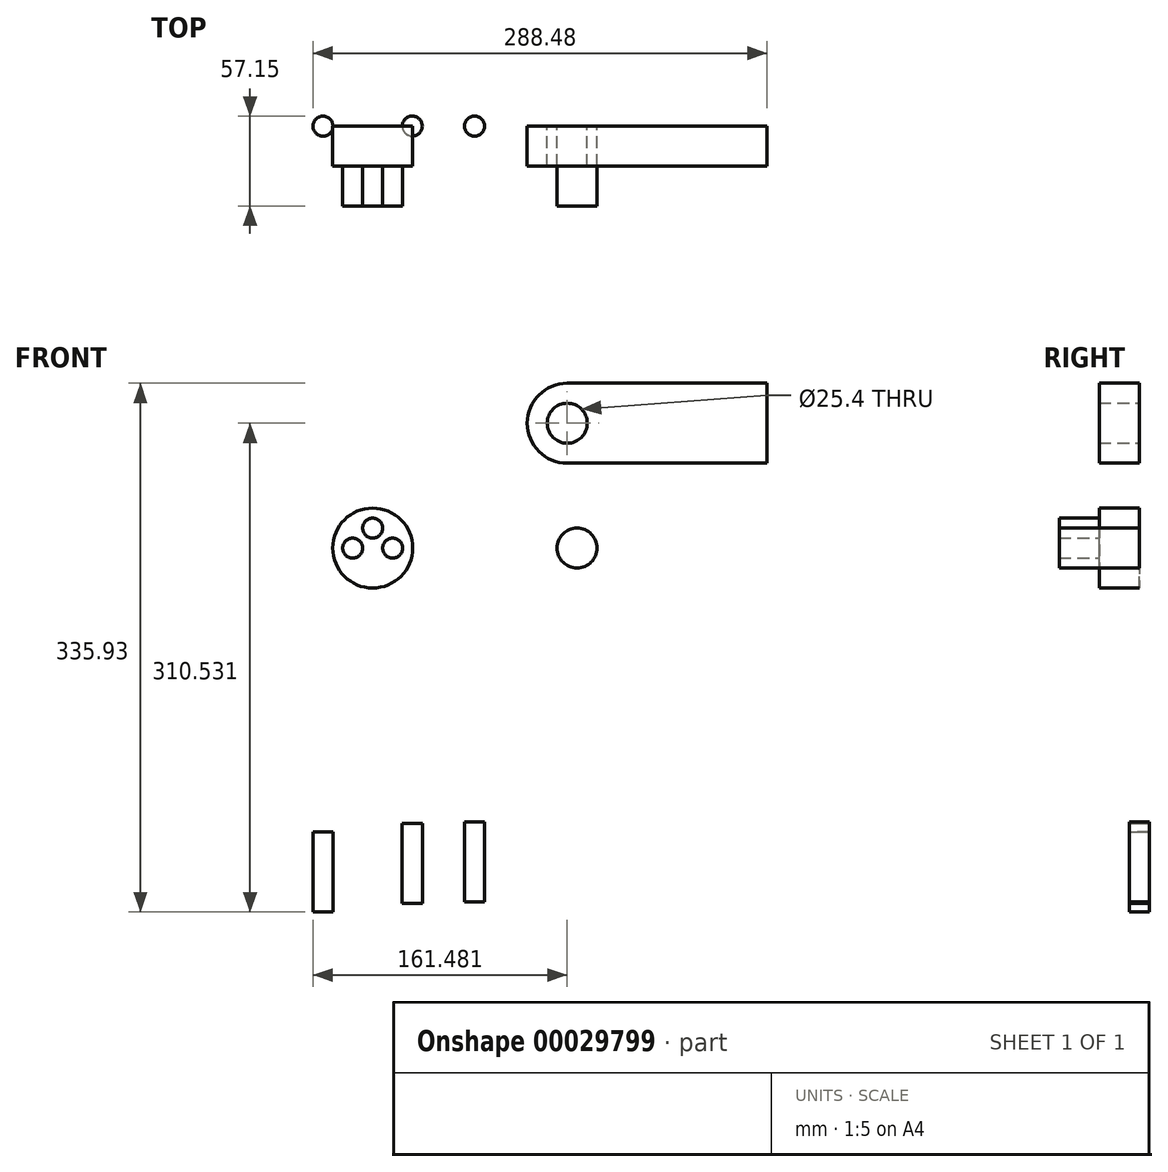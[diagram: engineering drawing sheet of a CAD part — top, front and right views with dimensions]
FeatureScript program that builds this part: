
annotation { "Feature Type Name" : "Feature", "Feature Type Description" : "" }
export const myFeature = defineFeature(function(context is Context, id is Id, definition is map)
    precondition{}
    {
        {
            var Q0;
            Q0=qCreatedBy(makeId("Front.planeOp"),FACE);
            var sketch = newSketch(context, id + "F0", { "sketchPlane" : qUnion([Q0])});
            skCircle(sketch, "E0", {"center": v(0, 0) * mm, "radius": 12.7 * mm});
            skLineSegment(sketch, "E1", {"start": v(0, 0) * mm, "end": v(0, 12.7) * mm});
            skLineSegment(sketch, "E2.bottom", {"start": v(-6.25, 104.71) * mm, "end": v(120.75, 104.71) * mm});
            skLineSegment(sketch, "E2.top", {"start": v(-6.25, 53.91) * mm, "end": v(120.75, 53.91) * mm});
            skLineSegment(sketch, "E2.left", {"start": v(-31.65, 79.31) * mm, "end": v(-31.65, 79.31) * mm});
            skLineSegment(sketch, "E2.right", {"start": v(120.75, 104.71) * mm, "end": v(120.75, 53.91) * mm});
            skPoint(sketch, "E3.visualSharp", {"position": v(-31.65, 104.71) * mm});
            skArc(sketch, "E3.filletArc", {"start": v(-6.25, 104.71) * mm, "mid": v(-24.2, 97.27) * mm, "end": v(-31.65, 79.31) * mm});
            skPoint(sketch, "E4.visualSharp", {"position": v(-31.65, 53.91) * mm});
            skArc(sketch, "E4.filletArc", {"start": v(-31.65, 79.31) * mm, "mid": v(-24.2, 61.35) * mm, "end": v(-6.25, 53.91) * mm});
            skCircle(sketch, "E5", {"center": v(-6.25, 79.31) * mm, "radius": 12.7 * mm});
            skLineSegment(sketch, "E6", {"start": v(-6.25, 79.31) * mm, "end": v(0, 90.37) * mm});
            skSolve(sketch);
        }
        {
            var Q0;
            Q0=makeQuery(id+"F0.imprint","IMPRINT",FACE,{"disambiguationData":[TD([[makeQuery(id+"F0.imprint","IMPRINT",EDGE,{"derivedFrom":sQuery(id+"F0.wireOp",EDGE,"E2.bottom")}),-1.0]])]});
            extrude(context, id + "F1", {"entities" : qUnion([Q0]), "depth" : 25.4 * mm});
        }
        {
            var Q0;
            Q0=qCreatedBy(makeId("Front.planeOp"),FACE);
            var sketch = newSketch(context, id + "F2", { "sketchPlane" : qUnion([Q0])});
            skLineSegment(sketch, "E7.bottom", {"start": v(-161.38, -180.42) * mm, "end": v(-155.03, -180.42) * mm});
            skLineSegment(sketch, "E7.top", {"start": v(-161.38, -231.22) * mm, "end": v(-155.03, -231.22) * mm});
            skLineSegment(sketch, "E7.left", {"start": v(-161.38, -180.42) * mm, "end": v(-161.38, -231.22) * mm});
            skLineSegment(sketch, "E7.right", {"start": v(-155.03, -180.42) * mm, "end": v(-155.03, -231.22) * mm});
            skLineSegment(sketch, "E8.bottom", {"start": v(-104.67, -225.58) * mm, "end": v(-98.32, -225.58) * mm});
            skLineSegment(sketch, "E8.top", {"start": v(-104.67, -174.78) * mm, "end": v(-98.32, -174.78) * mm});
            skLineSegment(sketch, "E8.left", {"start": v(-104.67, -225.58) * mm, "end": v(-104.67, -174.78) * mm});
            skLineSegment(sketch, "E8.right", {"start": v(-98.32, -225.58) * mm, "end": v(-98.32, -174.78) * mm});
            skLineSegment(sketch, "E9.bottom", {"start": v(-58.8, -224.74) * mm, "end": v(-65.15, -224.74) * mm});
            skLineSegment(sketch, "E9.top", {"start": v(-58.8, -173.94) * mm, "end": v(-65.15, -173.94) * mm});
            skLineSegment(sketch, "E9.left", {"start": v(-58.8, -224.74) * mm, "end": v(-58.8, -173.94) * mm});
            skLineSegment(sketch, "E9.right", {"start": v(-65.15, -224.74) * mm, "end": v(-65.15, -173.94) * mm});
            skSolve(sketch);
        }
        {
            var Q0;
            Q0=makeQuery(id+"F2.imprint","IMPRINT",FACE,{"disambiguationData":[TD([[makeQuery(id+"F2.imprint","IMPRINT",EDGE,{"derivedFrom":sQuery(id+"F2.wireOp",EDGE,"E7.bottom")}),-1.0]])]});
            var Q1;
            Q1=sQuery(id+"F2.wireOp",EDGE,"E7.left");
            revolve(context, id + "F3", {"entities" : qUnion([Q0]), "axis" : qUnion([Q1]), "revolveType" : RevolveType.FULL});
        }
        {
            var Q0;
            Q0=makeQuery(id+"F2.imprint","IMPRINT",FACE,{"disambiguationData":[TD([[makeQuery(id+"F2.imprint","IMPRINT",EDGE,{"derivedFrom":sQuery(id+"F2.wireOp",EDGE,"E8.bottom")}),1.0]])]});
            var Q1;
            Q1=sQuery(id+"F2.wireOp",EDGE,"E8.left");
            revolve(context, id + "F4", {"entities" : qUnion([Q0]), "axis" : qUnion([Q1]), "revolveType" : RevolveType.FULL});
        }
        {
            var Q0;
            Q0=makeQuery(id+"F2.imprint","IMPRINT",FACE,{"disambiguationData":[TD([[makeQuery(id+"F2.imprint","IMPRINT",EDGE,{"derivedFrom":sQuery(id+"F2.wireOp",EDGE,"E9.bottom")}),-1.0]])]});
            var Q1;
            Q1=sQuery(id+"F2.wireOp",EDGE,"E9.right");
            revolve(context, id + "F5", {"entities" : qUnion([Q0]), "axis" : qUnion([Q1]), "revolveType" : RevolveType.FULL});
        }
        {
            var Q0;
            Q0=makeQuery(id+"F0.imprint","IMPRINT",FACE,{"disambiguationData":[TD([[makeQuery(id+"F0.imprint","IMPRINT",EDGE,{"derivedFrom":sQuery(id+"F0.wireOp",EDGE,"E0")}),1.0]])]});
            extrude(context, id + "F6", {"entities" : qUnion([Q0]), "depth" : 50.8 * mm});
        }
        {
            var Q0;
            Q0=qCreatedBy(makeId("Front.planeOp"),FACE);
            var sketch = newSketch(context, id + "F7", { "sketchPlane" : qUnion([Q0])});
            skCircle(sketch, "E10", {"center": v(-129.83, 0) * mm, "radius": 25.4 * mm});
            skLineSegment(sketch, "E11", {"start": v(-129.83, 0) * mm, "end": v(-129.83, 25.4) * mm});
            skLineSegment(sketch, "E12", {"start": v(-129.83, 0) * mm, "end": v(-104.43, 0) * mm});
            skLineSegment(sketch, "E13", {"start": v(-129.83, 0) * mm, "end": v(-155.23, 0) * mm});
            skLineSegment(sketch, "E14", {"start": v(-129.83, 0) * mm, "end": v(-129.83, -25.4) * mm});
            skCircle(sketch, "E15", {"center": v(-129.83, 12.7) * mm, "radius": 6.35 * mm});
            skCircle(sketch, "E16", {"center": v(-117.13, 0) * mm, "radius": 6.35 * mm});
            skCircle(sketch, "E17", {"center": v(-142.53, 0) * mm, "radius": 6.35 * mm});
            skLineSegment(sketch, "E18", {"start": v(-142.53, 0) * mm, "end": v(-142.53, 6.35) * mm});
            skLineSegment(sketch, "E19", {"start": v(-129.83, 12.7) * mm, "end": v(-123.48, 12.7) * mm});
            skLineSegment(sketch, "E20", {"start": v(-117.13, 0) * mm, "end": v(-117.13, 6.35) * mm});
            skSolve(sketch);
        }
        {
            var Q0;
            {var subQ6=sQuery(id+"F7.wireOp",EDGE,"E11");var subQ10=sQuery(id+"F7.wireOp",EDGE,"E10");var subQ13=makeQuery(id+"F7.imprint","INTERSECT",VERTEX,{"derivedFrom":[subQ10,subQ6]});Q0=makeQuery(id+"F7.imprint","IMPRINT",FACE,{"disambiguationData":[TD([[makeQuery(id+"F7.imprint","IMPRINT",EDGE,{"disambiguationData":[TD([[subQ13,1.0]])],"derivedFrom":subQ10}),1.0]])]});}
            var Q1;
            {var subQ4=sQuery(id+"F7.wireOp",EDGE,"E14");Q1=makeQuery(id+"F7.imprint","IMPRINT",FACE,{"disambiguationData":[TD([[makeQuery(id+"F7.imprint","IMPRINT",EDGE,{"derivedFrom":subQ4}),1.0]])]});}
            var Q2;
            {var subQ4=sQuery(id+"F7.wireOp",EDGE,"E14");Q2=makeQuery(id+"F7.imprint","IMPRINT",FACE,{"disambiguationData":[TD([[makeQuery(id+"F7.imprint","IMPRINT",EDGE,{"derivedFrom":subQ4}),-1.0]])]});}
            var Q3;
            {var subQ6=sQuery(id+"F7.wireOp",EDGE,"E11");var subQ9=sQuery(id+"F7.wireOp",EDGE,"E10");var subQ12=makeQuery(id+"F7.imprint","INTERSECT",VERTEX,{"derivedFrom":[subQ9,subQ6]});Q3=makeQuery(id+"F7.imprint","IMPRINT",FACE,{"disambiguationData":[TD([[makeQuery(id+"F7.imprint","IMPRINT",EDGE,{"disambiguationData":[TD([[subQ12,-1.0]])],"derivedFrom":subQ9}),1.0]])]});}
            extrude(context, id + "F8", {"entities" : qUnion([Q0, Q1, Q2, Q3]), "depth" : 25.4 * mm});
        }
        {
            var Q0;
            {var subQ0=sQuery(id+"F7.wireOp",EDGE,"E20");Q0=makeQuery(id+"F7.imprint","IMPRINT",FACE,{"disambiguationData":[TD([[makeQuery(id+"F7.imprint","IMPRINT",EDGE,{"derivedFrom":subQ0}),-1.0]])]});}
            var Q1;
            {var subQ0=sQuery(id+"F7.wireOp",EDGE,"E20");Q1=makeQuery(id+"F7.imprint","IMPRINT",FACE,{"disambiguationData":[TD([[makeQuery(id+"F7.imprint","IMPRINT",EDGE,{"derivedFrom":subQ0}),1.0]])]});}
            var Q2;
            {var subQ1=sQuery(id+"F7.wireOp",EDGE,"E12");var subQ4=makeQuery(id+"F7.imprint","INTERSECT",VERTEX,{"derivedFrom":[subQ1,sQuery(id+"F7.wireOp",EDGE,"E20")]});Q2=makeQuery(id+"F7.imprint","IMPRINT",FACE,{"disambiguationData":[TD([[makeQuery(id+"F7.imprint","IMPRINT",EDGE,{"disambiguationData":[TD([[subQ4,1.0]])],"derivedFrom":subQ1}),-1.0]])]});}
            var Q3;
            {var subQ0=sQuery(id+"F7.wireOp",EDGE,"E19");Q3=makeQuery(id+"F7.imprint","IMPRINT",FACE,{"disambiguationData":[TD([[makeQuery(id+"F7.imprint","IMPRINT",EDGE,{"derivedFrom":subQ0}),1.0]])]});}
            var Q4;
            {var subQ1=sQuery(id+"F7.wireOp",EDGE,"E11");var subQ4=makeQuery(id+"F7.imprint","INTERSECT",VERTEX,{"derivedFrom":[subQ1,sQuery(id+"F7.wireOp",EDGE,"E19")]});Q4=makeQuery(id+"F7.imprint","IMPRINT",FACE,{"disambiguationData":[TD([[makeQuery(id+"F7.imprint","IMPRINT",EDGE,{"disambiguationData":[TD([[subQ4,1.0]])],"derivedFrom":subQ1}),1.0]])]});}
            var Q5;
            {var subQ0=sQuery(id+"F7.wireOp",EDGE,"E19");Q5=makeQuery(id+"F7.imprint","IMPRINT",FACE,{"disambiguationData":[TD([[makeQuery(id+"F7.imprint","IMPRINT",EDGE,{"derivedFrom":subQ0}),-1.0]])]});}
            var Q6;
            {var subQ0=sQuery(id+"F7.wireOp",EDGE,"E18");Q6=makeQuery(id+"F7.imprint","IMPRINT",FACE,{"disambiguationData":[TD([[makeQuery(id+"F7.imprint","IMPRINT",EDGE,{"derivedFrom":subQ0}),-1.0]])]});}
            var Q7;
            {var subQ0=sQuery(id+"F7.wireOp",EDGE,"E18");Q7=makeQuery(id+"F7.imprint","IMPRINT",FACE,{"disambiguationData":[TD([[makeQuery(id+"F7.imprint","IMPRINT",EDGE,{"derivedFrom":subQ0}),1.0]])]});}
            var Q8;
            {var subQ1=sQuery(id+"F7.wireOp",EDGE,"E13");var subQ4=makeQuery(id+"F7.imprint","INTERSECT",VERTEX,{"derivedFrom":[subQ1,sQuery(id+"F7.wireOp",EDGE,"E18")]});Q8=makeQuery(id+"F7.imprint","IMPRINT",FACE,{"disambiguationData":[TD([[makeQuery(id+"F7.imprint","IMPRINT",EDGE,{"disambiguationData":[TD([[subQ4,1.0]])],"derivedFrom":subQ1}),1.0]])]});}
            extrude(context, id + "F9", {"entities" : qUnion([Q0, Q1, Q2, Q3, Q4, Q5, Q6, Q7, Q8]), "operationType" : NewBodyOperationType.ADD, "depth" : 50.8 * mm});
        }
    });
